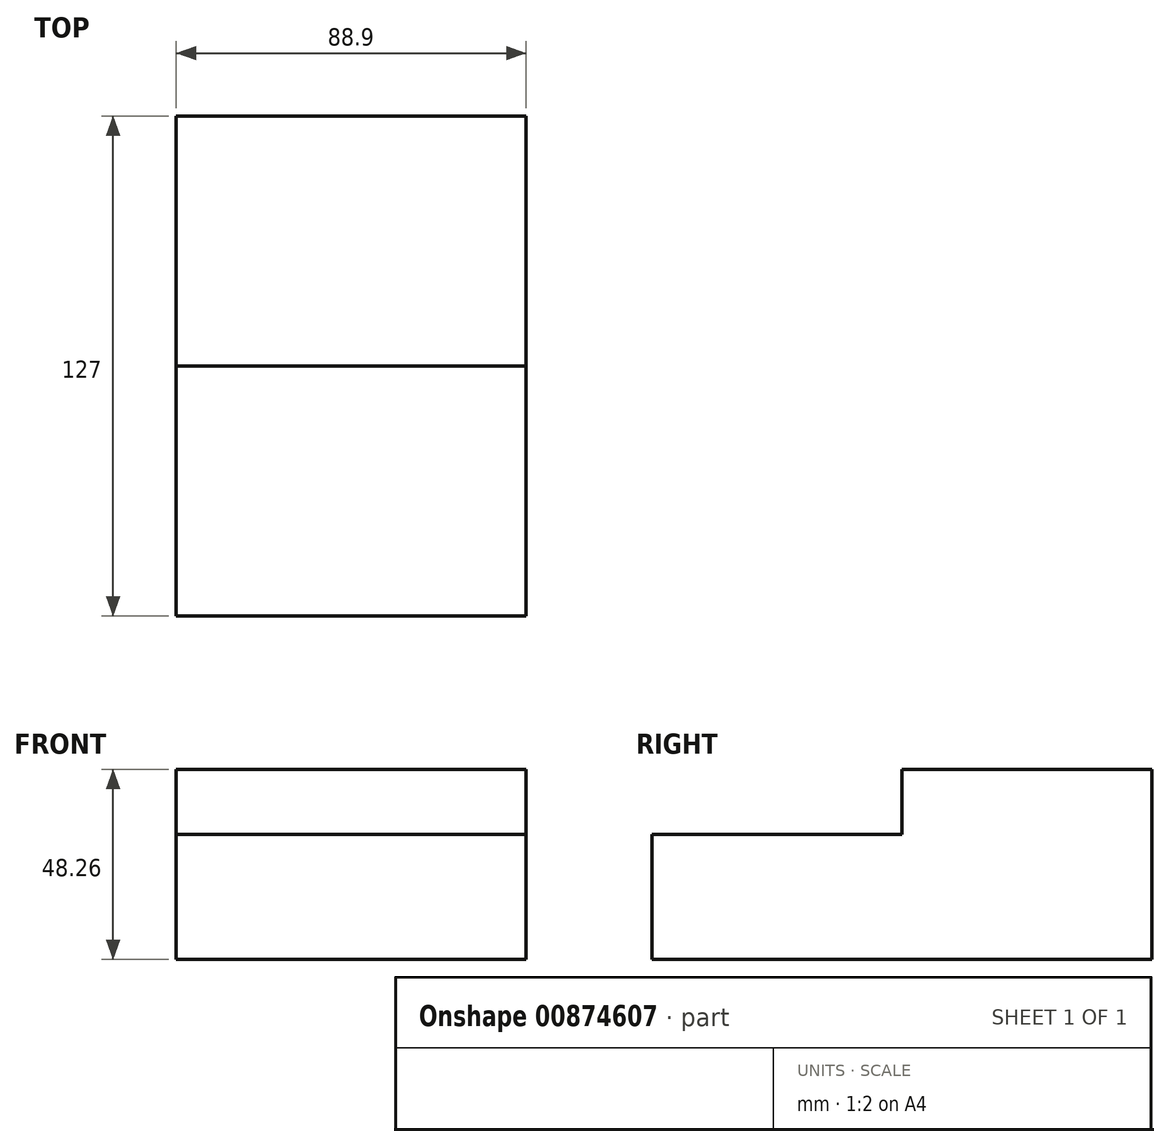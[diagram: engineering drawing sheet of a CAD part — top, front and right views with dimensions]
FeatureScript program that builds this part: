
annotation { "Feature Type Name" : "Feature", "Feature Type Description" : "" }
export const myFeature = defineFeature(function(context is Context, id is Id, definition is map)
    precondition{}
    {
        {
            var Q0;
            Q0=qCreatedBy(makeId("Top.planeOp"),FACE);
            var sketch = newSketch(context, id + "F0", { "sketchPlane" : qUnion([Q0])});
            skLineSegment(sketch, "E0.bottom", {"start": v(-44.82, 70.03) * mm, "end": v(44.08, 70.03) * mm});
            skLineSegment(sketch, "E0.top", {"start": v(-44.82, -56.97) * mm, "end": v(44.08, -56.97) * mm});
            skLineSegment(sketch, "E0.left", {"start": v(-44.82, 70.03) * mm, "end": v(-44.82, -56.97) * mm});
            skLineSegment(sketch, "E0.right", {"start": v(44.08, 70.03) * mm, "end": v(44.08, -56.97) * mm});
            skSolve(sketch);
        }
        {
            var Q0;
            Q0=makeQuery(id+"F0.imprint","IMPRINT",FACE,{"disambiguationData":[TD([[makeQuery(id+"F0.imprint","IMPRINT",EDGE,{"derivedFrom":sQuery(id+"F0.wireOp",EDGE,"E0.bottom")}),-1.0]])]});
            extrude(context, id + "F1", {"entities" : qUnion([Q0]), "depth" : 63.5 * mm, "offsetDistance" : 25.4 * mm});
        }
        {
            var Q0;
            Q0=makeQuery(id+"F1.opExtrude","CAP_FACE",FACE,{"disambiguationData":[OSD([sQuery(id+"F0.wireOp",EDGE,"E0.bottom"),sQuery(id+"F0.wireOp",EDGE,"E0.top"),sQuery(id+"F0.wireOp",EDGE,"E0.left"),sQuery(id+"F0.wireOp",EDGE,"E0.right")])],"isStart":false});
            var sketch = newSketch(context, id + "F2", { "sketchPlane" : qUnion([Q0])});
            skLineSegment(sketch, "E1", {"start": v(-44.82, 70.03) * mm, "end": v(-44.82, 6.53) * mm});
            skLineSegment(sketch, "E2", {"start": v(44.08, 6.53) * mm, "end": v(-44.82, 6.53) * mm});
            skLineSegment(sketch, "E3", {"start": v(-44.82, 6.53) * mm, "end": v(5.98, 6.53) * mm});
            skLineSegment(sketch, "E4", {"start": v(5.98, 6.53) * mm, "end": v(5.98, 70.03) * mm});
            skLineSegment(sketch, "E5", {"start": v(44.08, 70.03) * mm, "end": v(5.98, 70.03) * mm});
            skLineSegment(sketch, "E6", {"start": v(44.08, 70.03) * mm, "end": v(44.08, 6.53) * mm});
            skSolve(sketch);
        }
        {
            var Q0;
            Q0=makeQuery(id+"F2.imprint","IMPRINT",FACE,{"disambiguationData":[TD([[makeQuery(id+"F2.imprint","IMPRINT",EDGE,{"derivedFrom":sQuery(id+"F2.wireOp",EDGE,"E2")}),-1.0]])]});
            extrude(context, id + "F3", {"entities" : qUnion([Q0]), "operationType" : NewBodyOperationType.REMOVE, "oppositeDirection" : true, "depth" : 15.24 * mm, "offsetDistance" : 25.4 * mm});
        }
        {
            var Q0;
            Q0=makeQuery(id+"F1.opExtrude","CAP_FACE",FACE,{"disambiguationData":[OSD([sQuery(id+"F0.wireOp",EDGE,"E0.bottom"),sQuery(id+"F0.wireOp",EDGE,"E0.top"),sQuery(id+"F0.wireOp",EDGE,"E0.left"),sQuery(id+"F0.wireOp",EDGE,"E0.right")])],"isStart":false});
            var sketch = newSketch(context, id + "F4", { "sketchPlane" : qUnion([Q0])});
            skLineSegment(sketch, "E7", {"start": v(5.98, 6.53) * mm, "end": v(-44.82, 6.53) * mm});
            skSolve(sketch);
        }
        {
            var Q0;
            {var subQ1=sQuery(id+"F4.wireOp",EDGE,"E7");Q0=makeQuery(id+"F4.imprint","IMPRINT",FACE,{"disambiguationData":[TD([[makeQuery(id+"F4.imprint","IMPRINT",EDGE,{"derivedFrom":subQ1}),1.0]])]});}
            extrude(context, id + "F5", {"entities" : qUnion([Q0]), "operationType" : NewBodyOperationType.REMOVE, "oppositeDirection" : true, "depth" : 31.75 * mm, "offsetDistance" : 25.4 * mm});
        }
    });
